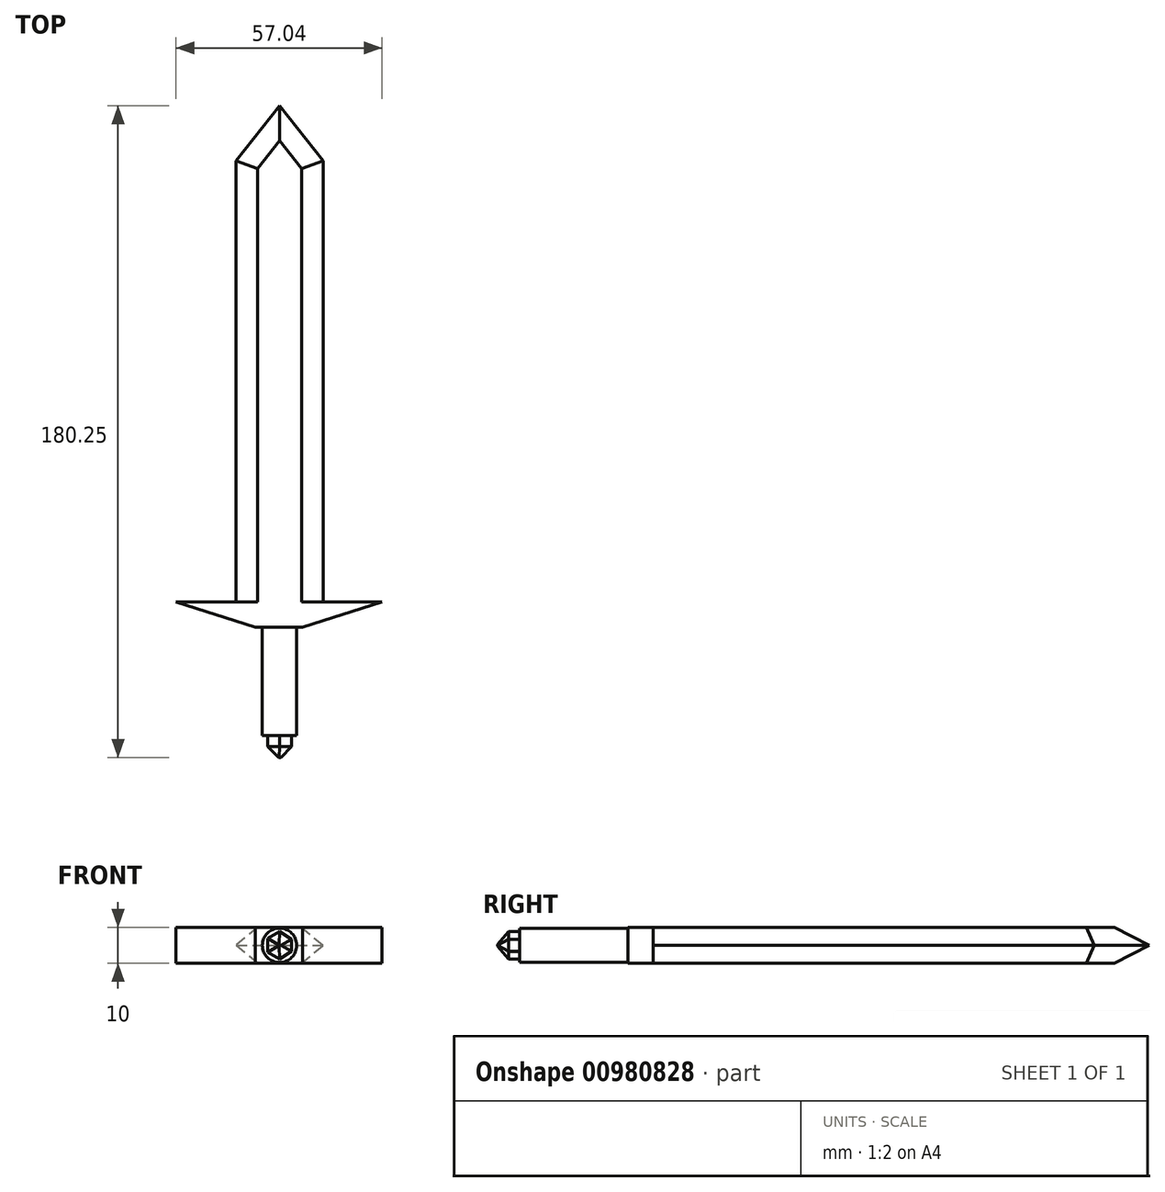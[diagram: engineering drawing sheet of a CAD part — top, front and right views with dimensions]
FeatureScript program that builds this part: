
annotation { "Feature Type Name" : "Feature", "Feature Type Description" : "" }
export const myFeature = defineFeature(function(context is Context, id is Id, definition is map)
    precondition{}
    {
        {
            var Q0;
            Q0=qCreatedBy(makeId("Top.planeOp"),FACE);
            var sketch = newSketch(context, id + "F0", { "sketchPlane" : qUnion([Q0])});
            skLineSegment(sketch, "E0.top", {"start": v(-12.05, -68.62) * mm, "end": v(12.05, -68.62) * mm});
            skLineSegment(sketch, "E0.left", {"start": v(-12.05, 53.37) * mm, "end": v(-12.05, -68.62) * mm});
            skLineSegment(sketch, "E0.right", {"start": v(12.05, 53.37) * mm, "end": v(12.05, -68.62) * mm});
            skPoint(sketch, "E0.middle", {"position": v(0, 0) * mm});
            skLineSegment(sketch, "E1", {"start": v(-12.05, 53.37) * mm, "end": v(0, 68.62) * mm});
            skLineSegment(sketch, "E2", {"start": v(0, 68.62) * mm, "end": v(12.05, 53.37) * mm});
            skPoint(sketch, "E3.orphan", {"position": v(-12.05, 68.62) * mm});
            skPoint(sketch, "E4.orphan", {"position": v(12.05, 68.62) * mm});
            skLineSegment(sketch, "E5.bottom", {"start": v(-28.64, -68.62) * mm, "end": v(28.4, -68.62) * mm});
            skLineSegment(sketch, "E5.top", {"start": v(-6.68, -75.63) * mm, "end": v(6.43, -75.63) * mm});
            skLineSegment(sketch, "E6", {"start": v(-28.64, -68.62) * mm, "end": v(-6.68, -75.63) * mm});
            skLineSegment(sketch, "E7", {"start": v(6.43, -75.63) * mm, "end": v(28.4, -68.62) * mm});
            skSolve(sketch);
        }
        {
            var Q0;
            {var subQ1=sQuery(id+"F0.wireOp",EDGE,"E0.left");Q0=makeQuery(id+"F0.imprint","IMPRINT",FACE,{"disambiguationData":[TD([[makeQuery(id+"F0.imprint","IMPRINT",EDGE,{"derivedFrom":subQ1}),1.0]])]});}
            var Q1;
            Q1=makeQuery(id+"F0.imprint","IMPRINT",FACE,{"disambiguationData":[TD([[makeQuery(id+"F0.imprint","IMPRINT",EDGE,{"derivedFrom":sQuery(id+"F0.wireOp",EDGE,"E5.top")}),1.0]])]});
            extrude(context, id + "F1", {"entities" : qUnion([Q0, Q1]), "depth" : 5 * mm, "offsetDistance" : 25 * mm});
        }
        {
            var Q0;
            Q0=makeQuery(id+"F1.opExtrude","CAP_EDGE",EDGE,{"disambiguationData":[OSD([sQuery(id+"F0.wireOp",EDGE,"E0.right")])],"isStart":false});
            var Q1;
            Q1=makeQuery(id+"F1.opExtrude","CAP_EDGE",EDGE,{"disambiguationData":[OSD([sQuery(id+"F0.wireOp",EDGE,"E2")])],"isStart":false});
            var Q2;
            Q2=makeQuery(id+"F1.opExtrude","CAP_EDGE",EDGE,{"disambiguationData":[OSD([sQuery(id+"F0.wireOp",EDGE,"E1")])],"isStart":false});
            var Q3;
            Q3=makeQuery(id+"F1.opExtrude","CAP_EDGE",EDGE,{"disambiguationData":[OSD([sQuery(id+"F0.wireOp",EDGE,"E0.left")])],"isStart":false});
            chamfer(context, id + "F2", {"entities" : qUnion([Q0, Q1, Q2, Q3]), "chamferType" : ChamferType.OFFSET_ANGLE, "width" : 5 * mm, "oppositeDirection" : false, "angle" : 50 * degree, "tangentPropagation" : true});
        }
        {
            var Q0;
            Q0=makeQuery(id+"F1.opExtrude","SWEPT_BODY",BODY,{"disambiguationData":[OSD([sQuery(id+"F0.wireOp",EDGE,"E0.left"),sQuery(id+"F0.wireOp",EDGE,"E0.right"),sQuery(id+"F0.wireOp",EDGE,"E1"),sQuery(id+"F0.wireOp",EDGE,"E2"),sQuery(id+"F0.wireOp",EDGE,"E5.bottom"),sQuery(id+"F0.wireOp",EDGE,"E5.top"),sQuery(id+"F0.wireOp",EDGE,"E6"),sQuery(id+"F0.wireOp",EDGE,"E7")])]});
            var Q1;
            Q1=qCreatedBy(makeId("Top.planeOp"),FACE);
            mirror(context, id + "F3", {"operationType" : NewBodyOperationType.ADD, "entities" : qUnion([Q0]), "mirrorPlane" : qUnion([Q1])});
        }
        {
            var Q0;
            {var subQ0=makeQuery(id+"F1.opExtrude","SWEPT_FACE",FACE,{"disambiguationData":[OSD([sQuery(id+"F0.wireOp",EDGE,"E5.top")])]});Q0=makeQuery(id+"F3.boolean.opBoolean","MERGE",FACE,{"derivedFrom":[subQ0,makeQuery(id+"F3.opPattern","COPY",FACE,{"derivedFrom":subQ0,"instanceName":"1"})]});}
            var sketch = newSketch(context, id + "F4", { "sketchPlane" : qUnion([Q0])});
            skCircle(sketch, "E8", {"center": v(0, 0) * mm, "radius": 4.75 * mm});
            skSolve(sketch);
        }
        {
            var Q0;
            Q0=makeQuery(id+"F4.imprint","IMPRINT",FACE,{"disambiguationData":[TD([[makeQuery(id+"F4.imprint","IMPRINT",EDGE,{"derivedFrom":sQuery(id+"F4.wireOp",EDGE,"E8")}),1.0]])]});
            var Q1;
            Q1=sQuery(id+"F4.wireOp",EDGE,"E8");
            extrude(context, id + "F5", {"entities" : qUnion([Q0]), "operationType" : NewBodyOperationType.ADD, "surfaceEntities" : qUnion([Q1]), "depth" : 30 * mm, "offsetDistance" : 25 * mm});
        }
        {
            var Q0;
            Q0=makeQuery(id+"F5.opExtrude","CAP_FACE",FACE,{"disambiguationData":[OSD([sQuery(id+"F4.wireOp",EDGE,"E8")])],"isStart":false});
            var sketch = newSketch(context, id + "F6", { "sketchPlane" : qUnion([Q0])});
            skLineSegment(sketch, "E9", {"start": v(0, 3.78) * mm, "end": v(3.4, 1.67) * mm});
            skLineSegment(sketch, "E10", {"start": v(3.4, 1.67) * mm, "end": v(3.4, -1.67) * mm});
            skLineSegment(sketch, "E11", {"start": v(3.4, -1.67) * mm, "end": v(0, -3.78) * mm});
            skLineSegment(sketch, "E12", {"start": v(0, -3.78) * mm, "end": v(-3.26, -1.92) * mm});
            skLineSegment(sketch, "E13", {"start": v(-3.26, -1.92) * mm, "end": v(-3.26, 1.92) * mm});
            skLineSegment(sketch, "E14", {"start": v(-3.26, 1.92) * mm, "end": v(0, 3.78) * mm});
            skSolve(sketch);
        }
        {
            var Q0;
            Q0=makeQuery(id+"F6.imprint","IMPRINT",FACE,{"disambiguationData":[TD([[makeQuery(id+"F6.imprint","IMPRINT",EDGE,{"derivedFrom":sQuery(id+"F6.wireOp",EDGE,"E9")}),-1.0]])]});
            extrude(context, id + "F7", {"entities" : qUnion([Q0]), "operationType" : NewBodyOperationType.ADD, "depth" : 6 * mm, "offsetDistance" : 25 * mm});
        }
        {
            var Q0;
            Q0=makeQuery(id+"F7.opExtrude","CAP_EDGE",EDGE,{"disambiguationData":[OSD([sQuery(id+"F6.wireOp",EDGE,"E14")])],"isStart":false});
            var Q1;
            Q1=makeQuery(id+"F7.opExtrude","CAP_EDGE",EDGE,{"disambiguationData":[OSD([sQuery(id+"F6.wireOp",EDGE,"E9")])],"isStart":false});
            var Q2;
            Q2=makeQuery(id+"F7.opExtrude","CAP_EDGE",EDGE,{"disambiguationData":[OSD([sQuery(id+"F6.wireOp",EDGE,"E13")])],"isStart":false});
            var Q3;
            Q3=makeQuery(id+"F7.opExtrude","CAP_EDGE",EDGE,{"disambiguationData":[OSD([sQuery(id+"F6.wireOp",EDGE,"E12")])],"isStart":false});
            var Q4;
            Q4=makeQuery(id+"F7.opExtrude","CAP_EDGE",EDGE,{"disambiguationData":[OSD([sQuery(id+"F6.wireOp",EDGE,"E11")])],"isStart":false});
            var Q5;
            Q5=makeQuery(id+"F7.opExtrude","CAP_EDGE",EDGE,{"disambiguationData":[OSD([sQuery(id+"F6.wireOp",EDGE,"E10")])],"isStart":false});
            chamfer(context, id + "F8", {"entities" : qUnion([Q0, Q1, Q2, Q3, Q4, Q5]), "chamferType" : ChamferType.OFFSET_ANGLE, "width" : 3 * mm, "oppositeDirection" : false, "angle" : 45 * degree, "tangentPropagation" : true});
        }
    });
